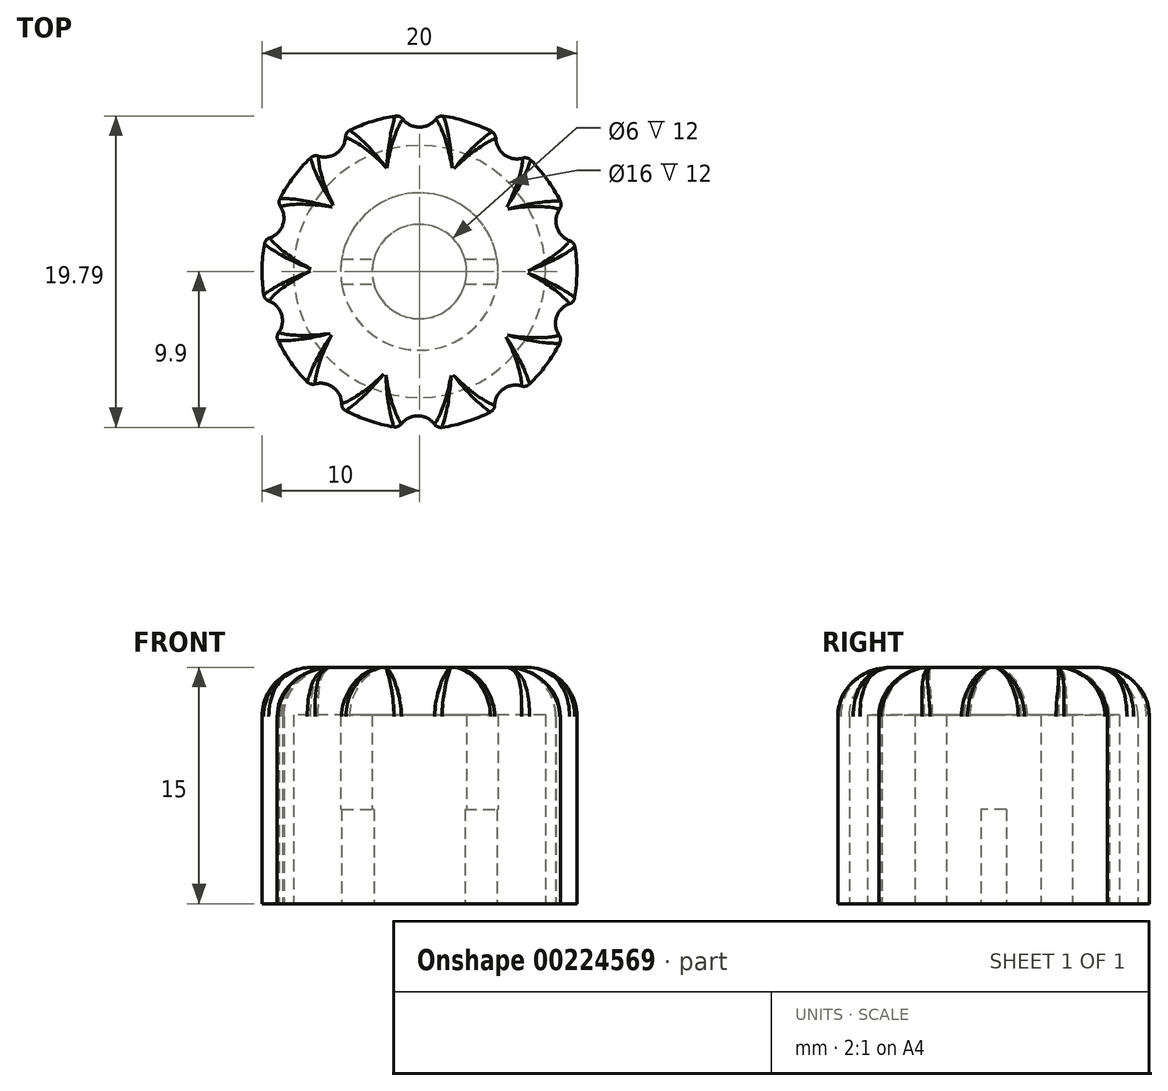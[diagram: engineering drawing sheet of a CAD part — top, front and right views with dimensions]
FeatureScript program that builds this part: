
annotation { "Feature Type Name" : "Feature", "Feature Type Description" : "" }
export const myFeature = defineFeature(function(context is Context, id is Id, definition is map)
    precondition{}
    {
        {
            var Q0;
            Q0=qCreatedBy(makeId("Top.planeOp"),FACE);
            var sketch = newSketch(context, id + "F0", { "sketchPlane" : qUnion([Q0])});
            skCircle(sketch, "E0", {"center": v(0, 0) * mm, "radius": 3 * mm});
            skArc(sketch, "E1", {"start": v(-1.53, 9.88) * mm, "mid": v(-3, 9.54) * mm, "end": v(-4.42, 8.97) * mm});
            skArc(sketch, "E2", {"start": v(-1.06, 9.7) * mm, "mid": v(0, 9.17) * mm, "end": v(1.06, 9.7) * mm});
            skPoint(sketch, "E3.visualSharp", {"position": v(-1.2, 9.93) * mm});
            skArc(sketch, "E3.filletArc", {"start": v(-1.06, 9.7) * mm, "mid": v(-1.27, 9.85) * mm, "end": v(-1.53, 9.88) * mm});
            skPoint(sketch, "E4.visualSharp", {"position": v(1.2, 9.93) * mm});
            skArc(sketch, "E4.filletArc", {"start": v(1.53, 9.88) * mm, "mid": v(1.27, 9.85) * mm, "end": v(1.06, 9.7) * mm});
            skArc(sketch, "E5.1.0", {"start": v(4.86, 8.45) * mm, "mid": v(5.4, 7.4) * mm, "end": v(6.57, 7.2) * mm});
            skPoint(sketch, "E5.1.1", {"position": v(6.82, 7.31) * mm});
            skPoint(sketch, "E5.1.2", {"position": v(4.88, 8.73) * mm});
            skArc(sketch, "E5.1.3", {"start": v(4.86, 8.45) * mm, "mid": v(4.78, 8.7) * mm, "end": v(4.59, 8.89) * mm});
            skArc(sketch, "E5.1.4", {"start": v(7.06, 7.08) * mm, "mid": v(6.83, 7.21) * mm, "end": v(6.57, 7.2) * mm});
            skArc(sketch, "E5.2.0", {"start": v(8.9, 3.96) * mm, "mid": v(8.73, 2.8) * mm, "end": v(9.55, 1.95) * mm});
            skPoint(sketch, "E5.2.1", {"position": v(9.82, 1.89) * mm});
            skPoint(sketch, "E5.2.2", {"position": v(9.09, 4.17) * mm});
            skArc(sketch, "E5.2.3", {"start": v(8.9, 3.96) * mm, "mid": v(9, 4.21) * mm, "end": v(8.94, 4.47) * mm});
            skArc(sketch, "E5.2.4", {"start": v(9.88, 1.56) * mm, "mid": v(9.77, 1.8) * mm, "end": v(9.55, 1.95) * mm});
            skArc(sketch, "E5.3.0", {"start": v(9.53, -2.05) * mm, "mid": v(8.7, -2.88) * mm, "end": v(8.87, -4.05) * mm});
            skPoint(sketch, "E5.3.1", {"position": v(9.05, -4.26) * mm});
            skPoint(sketch, "E5.3.2", {"position": v(9.8, -1.98) * mm});
            skArc(sketch, "E5.3.3", {"start": v(9.53, -2.05) * mm, "mid": v(9.75, -1.9) * mm, "end": v(9.86, -1.66) * mm});
            skArc(sketch, "E5.3.4", {"start": v(8.9, -4.56) * mm, "mid": v(8.95, -4.3) * mm, "end": v(8.87, -4.05) * mm});
            skArc(sketch, "E5.4.0", {"start": v(6.5, -7.27) * mm, "mid": v(5.33, -7.46) * mm, "end": v(4.78, -8.5) * mm});
            skPoint(sketch, "E5.4.1", {"position": v(4.8, -8.77) * mm});
            skPoint(sketch, "E5.4.2", {"position": v(6.75, -7.38) * mm});
            skArc(sketch, "E5.4.3", {"start": v(6.5, -7.27) * mm, "mid": v(6.76, -7.28) * mm, "end": v(7, -7.15) * mm});
            skArc(sketch, "E5.4.4", {"start": v(4.5, -8.93) * mm, "mid": v(4.7, -8.75) * mm, "end": v(4.78, -8.5) * mm});
            skArc(sketch, "E5.5.0", {"start": v(0.96, -9.7) * mm, "mid": v(-0.09, -9.17) * mm, "end": v(-1.15, -9.68) * mm});
            skPoint(sketch, "E5.5.1", {"position": v(-1.3, -9.92) * mm});
            skPoint(sketch, "E5.5.2", {"position": v(1.1, -9.94) * mm});
            skArc(sketch, "E5.5.3", {"start": v(0.96, -9.7) * mm, "mid": v(1.17, -9.86) * mm, "end": v(1.43, -9.9) * mm});
            skArc(sketch, "E5.5.4", {"start": v(-1.63, -9.87) * mm, "mid": v(-1.36, -9.84) * mm, "end": v(-1.15, -9.68) * mm});
            skArc(sketch, "E5.6.0", {"start": v(-4.94, -8.4) * mm, "mid": v(-5.48, -7.36) * mm, "end": v(-6.63, -7.14) * mm});
            skPoint(sketch, "E5.6.1", {"position": v(-6.9, -7.25) * mm});
            skPoint(sketch, "E5.6.2", {"position": v(-4.97, -8.68) * mm});
            skArc(sketch, "E5.6.3", {"start": v(-4.94, -8.4) * mm, "mid": v(-4.87, -8.66) * mm, "end": v(-4.67, -8.84) * mm});
            skArc(sketch, "E5.6.4", {"start": v(-7.13, -7.01) * mm, "mid": v(-6.9, -7.15) * mm, "end": v(-6.63, -7.14) * mm});
            skArc(sketch, "E5.7.0", {"start": v(-8.94, -3.88) * mm, "mid": v(-8.76, -2.72) * mm, "end": v(-9.57, -1.86) * mm});
            skPoint(sketch, "E5.7.1", {"position": v(-9.84, -1.8) * mm});
            skPoint(sketch, "E5.7.2", {"position": v(-9.13, -4.09) * mm});
            skArc(sketch, "E5.7.3", {"start": v(-8.94, -3.88) * mm, "mid": v(-9.04, -4.13) * mm, "end": v(-8.99, -4.39) * mm});
            skArc(sketch, "E5.7.4", {"start": v(-9.9, -1.47) * mm, "mid": v(-9.79, -1.7) * mm, "end": v(-9.57, -1.86) * mm});
            skArc(sketch, "E5.8.0", {"start": v(-9.51, 2.14) * mm, "mid": v(-8.68, 2.97) * mm, "end": v(-8.83, 4.14) * mm});
            skPoint(sketch, "E5.8.1", {"position": v(-9, 4.35) * mm});
            skPoint(sketch, "E5.8.2", {"position": v(-9.78, 2.08) * mm});
            skArc(sketch, "E5.8.3", {"start": v(-9.51, 2.14) * mm, "mid": v(-9.73, 2) * mm, "end": v(-9.85, 1.75) * mm});
            skArc(sketch, "E5.8.4", {"start": v(-8.86, 4.65) * mm, "mid": v(-8.91, 4.39) * mm, "end": v(-8.83, 4.14) * mm});
            skArc(sketch, "E5.9.0", {"start": v(-6.42, 7.33) * mm, "mid": v(-5.26, 7.51) * mm, "end": v(-4.7, 8.54) * mm});
            skPoint(sketch, "E5.9.1", {"position": v(-4.71, 8.82) * mm});
            skPoint(sketch, "E5.9.2", {"position": v(-6.68, 7.44) * mm});
            skArc(sketch, "E5.9.3", {"start": v(-6.42, 7.33) * mm, "mid": v(-6.69, 7.34) * mm, "end": v(-6.92, 7.22) * mm});
            skArc(sketch, "E5.9.4", {"start": v(-4.42, 8.97) * mm, "mid": v(-4.61, 8.8) * mm, "end": v(-4.7, 8.54) * mm});
            skLineSegment(sketch, "E5.anchor1", {"start": v(0, 0) * mm, "end": v(-1.45, 9.39) * mm, "construction": true});
            skLineSegment(sketch, "E5.anchor2", {"start": v(0, 0) * mm, "end": v(-6.58, 6.86) * mm, "construction": true});
            skArc(sketch, "E6.trimOffspring", {"start": v(-6.92, 7.22) * mm, "mid": v(-8, 6.01) * mm, "end": v(-8.86, 4.65) * mm});
            skArc(sketch, "E7.trimOffspring", {"start": v(-9.85, 1.75) * mm, "mid": v(-10, 0.15) * mm, "end": v(-9.9, -1.47) * mm});
            skArc(sketch, "E8.trimOffspring", {"start": v(-8.99, -4.39) * mm, "mid": v(-8.16, -5.78) * mm, "end": v(-7.13, -7.01) * mm});
            skArc(sketch, "E9.trimOffspring", {"start": v(-4.67, -8.84) * mm, "mid": v(-3.2, -9.48) * mm, "end": v(-1.63, -9.87) * mm});
            skArc(sketch, "E10.trimOffspring", {"start": v(1.43, -9.9) * mm, "mid": v(3, -9.54) * mm, "end": v(4.5, -8.93) * mm});
            skArc(sketch, "E11.trimOffspring", {"start": v(7, -7.15) * mm, "mid": v(8.05, -5.93) * mm, "end": v(8.9, -4.56) * mm});
            skArc(sketch, "E12.trimOffspring", {"start": v(9.86, -1.66) * mm, "mid": v(10, -0.05) * mm, "end": v(9.88, 1.56) * mm});
            skArc(sketch, "E13.trimOffspring", {"start": v(8.94, 4.47) * mm, "mid": v(8.1, 5.85) * mm, "end": v(7.06, 7.08) * mm});
            skArc(sketch, "E14.trimOffspring", {"start": v(4.59, 8.89) * mm, "mid": v(3.1, 9.5) * mm, "end": v(1.53, 9.88) * mm});
            skCircle(sketch, "E15.0", {"center": v(0, 0) * mm, "radius": 5 * mm});
            skCircle(sketch, "E16.0", {"center": v(0, 0) * mm, "radius": 8 * mm});
            skLineSegment(sketch, "E17", {"start": v(-11.37, 0) * mm, "end": v(12.27, 0) * mm, "construction": true});
            skLineSegment(sketch, "E18.0", {"start": v(-4.94, -0.8) * mm, "end": v(-2.9, -0.8) * mm});
            skLineSegment(sketch, "E19.MirrorCS", {"start": v(-4.94, 0.8) * mm, "end": v(-2.9, 0.8) * mm});
            skPoint(sketch, "E20.orphan", {"position": v(-11.37, 0.8) * mm});
            skPoint(sketch, "E21.orphan", {"position": v(-11.37, -0.8) * mm});
            skLineSegment(sketch, "E22.trimOffspring", {"start": v(2.9, 0.8) * mm, "end": v(4.94, 0.8) * mm});
            skLineSegment(sketch, "E23.trimOffspring", {"start": v(2.9, -0.8) * mm, "end": v(4.94, -0.8) * mm});
            skPoint(sketch, "E24.trimOffspring.end.orphan", {"position": v(12.27, 0.8) * mm});
            skPoint(sketch, "E25.trimOffspring.end.orphan", {"position": v(12.27, -0.8) * mm});
            skSolve(sketch);
        }
        {
            var Q0;
            Q0=makeQuery(id+"F0.imprint","IMPRINT",FACE,{"disambiguationData":[TD([[makeQuery(id+"F0.imprint","IMPRINT",EDGE,{"derivedFrom":sQuery(id+"F0.wireOp",EDGE,"E0")}),-1.0]])]});
            var Q1;
            Q1=makeQuery(id+"F0.imprint","IMPRINT",FACE,{"disambiguationData":[TD([[makeQuery(id+"F0.imprint","IMPRINT",EDGE,{"derivedFrom":sQuery(id+"F0.wireOp",EDGE,"E0")}),1.0]])]});
            var Q2;
            Q2=makeQuery(id+"F0.imprint","IMPRINT",FACE,{"disambiguationData":[TD([[makeQuery(id+"F0.imprint","IMPRINT",EDGE,{"derivedFrom":sQuery(id+"F0.wireOp",EDGE,"E15.0")}),-1.0]])]});
            var Q3;
            Q3=makeQuery(id+"F0.imprint","IMPRINT",FACE,{"disambiguationData":[TD([[makeQuery(id+"F0.imprint","IMPRINT",EDGE,{"derivedFrom":sQuery(id+"F0.wireOp",EDGE,"E1")}),1.0]])]});
            extrude(context, id + "F1", {"entities" : qUnion([Q0, Q1, Q2, Q3]), "depth" : 15 * mm});
        }
        {
            var Q0;
            Q0=makeQuery(id+"F0.imprint","IMPRINT",FACE,{"disambiguationData":[TD([[makeQuery(id+"F0.imprint","IMPRINT",EDGE,{"derivedFrom":sQuery(id+"F0.wireOp",EDGE,"E0")}),1.0]])]});
            var Q1;
            Q1=makeQuery(id+"F0.imprint","IMPRINT",FACE,{"disambiguationData":[TD([[makeQuery(id+"F0.imprint","IMPRINT",EDGE,{"derivedFrom":sQuery(id+"F0.wireOp",EDGE,"E15.0")}),-1.0]])]});
            extrude(context, id + "F2", {"entities" : qUnion([Q0, Q1]), "operationType" : NewBodyOperationType.REMOVE, "depth" : 12 * mm});
        }
        {
            var Q0;
            {var subQ0=sQuery(id+"F0.wireOp",EDGE,"E18.0");Q0=makeQuery(id+"F0.imprint","IMPRINT",FACE,{"disambiguationData":[TD([[makeQuery(id+"F0.imprint","IMPRINT",EDGE,{"derivedFrom":subQ0}),1.0]])]});}
            var Q1;
            {var subQ0=sQuery(id+"F0.wireOp",EDGE,"E22.trimOffspring");Q1=makeQuery(id+"F0.imprint","IMPRINT",FACE,{"disambiguationData":[TD([[makeQuery(id+"F0.imprint","IMPRINT",EDGE,{"derivedFrom":subQ0}),-1.0]])]});}
            extrude(context, id + "F3", {"entities" : qUnion([Q0, Q1]), "operationType" : NewBodyOperationType.REMOVE, "depth" : 6 * mm});
        }
        {
            var Q0;
            Q0=makeQuery(id+"F1.opExtrude","CAP_EDGE",EDGE,{"disambiguationData":[OSD([sQuery(id+"F0.wireOp",EDGE,"E9.trimOffspring")])],"isStart":false});
            var Q1;
            Q1=makeQuery(id+"F1.opExtrude","CAP_EDGE",EDGE,{"disambiguationData":[OSD([sQuery(id+"F0.wireOp",EDGE,"E8.trimOffspring")])],"isStart":false});
            var Q2;
            Q2=makeQuery(id+"F1.opExtrude","CAP_EDGE",EDGE,{"disambiguationData":[OSD([sQuery(id+"F0.wireOp",EDGE,"E7.trimOffspring")])],"isStart":false});
            var Q3;
            Q3=makeQuery(id+"F1.opExtrude","CAP_EDGE",EDGE,{"disambiguationData":[OSD([sQuery(id+"F0.wireOp",EDGE,"E6.trimOffspring")])],"isStart":false});
            var Q4;
            Q4=makeQuery(id+"F1.opExtrude","CAP_EDGE",EDGE,{"disambiguationData":[OSD([sQuery(id+"F0.wireOp",EDGE,"E1")])],"isStart":false});
            var Q5;
            Q5=makeQuery(id+"F1.opExtrude","CAP_EDGE",EDGE,{"disambiguationData":[OSD([sQuery(id+"F0.wireOp",EDGE,"E14.trimOffspring")])],"isStart":false});
            var Q6;
            Q6=makeQuery(id+"F1.opExtrude","CAP_EDGE",EDGE,{"disambiguationData":[OSD([sQuery(id+"F0.wireOp",EDGE,"E13.trimOffspring")])],"isStart":false});
            var Q7;
            Q7=makeQuery(id+"F1.opExtrude","CAP_EDGE",EDGE,{"disambiguationData":[OSD([sQuery(id+"F0.wireOp",EDGE,"E12.trimOffspring")])],"isStart":false});
            var Q8;
            Q8=makeQuery(id+"F1.opExtrude","CAP_EDGE",EDGE,{"disambiguationData":[OSD([sQuery(id+"F0.wireOp",EDGE,"E11.trimOffspring")])],"isStart":false});
            var Q9;
            Q9=makeQuery(id+"F1.opExtrude","CAP_EDGE",EDGE,{"disambiguationData":[OSD([sQuery(id+"F0.wireOp",EDGE,"E10.trimOffspring")])],"isStart":false});
            fillet(context, id + "F4", {"entities" : qUnion([Q0, Q1, Q2, Q3, Q4, Q5, Q6, Q7, Q8, Q9]), "radius" : 3.1 * mm, "tangentPropagation" : true, "allowEdgeOverflow" : false});
        }
    });
